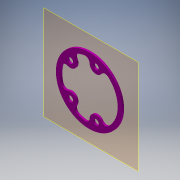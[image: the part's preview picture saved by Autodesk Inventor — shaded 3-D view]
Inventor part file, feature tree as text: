
AUTODESK INVENTOR PART (.ipt)
format: ipt  version: 2017 (Build 210142000, 142)  size: 202,752 bytes
history: native  units: in
note: dims shown in document units (in); Inventor stores cm internally (conversion verified against a paired STEP export)
features: other x4, reference x3, extrude x2, sketch x2, plane x1, fillet x1
ambient origin geometry x8: Origin, YZ Plane, XZ Plane, XY Plane, X Axis, Y Axis, Z Axis, Center Point
bodies: Solid1 (feature_tree)
feature tree (13):
  plane  "Work Plane1"
  extrude  "Extrusion1"  Depth=0.1in
  fillet  "Fillet1"  Radius=0.1in
  extrude  "Extrusion2"  Depth=0.085in
  sketch  "Sketch1"  dims[d0=0.1in d1=0.1in d2=0.1in]
  reference  "Reference1"
  reference  "Reference2"
  sketch  "Sketch2"  dims[d3=0.1in d4=0.15in d5=0.1in d6=0.15in d7=0.05in d8=0.125in d9=0.1in d10=0.125in d11=0.125in d12=0.125in d13=0.125in d14=0.05in d15=0.0in d16=0.125in d17=0.02in d18=0.085in d19=0.0in]
  reference  "Reference3"
  other  "<userpath>\Documents\Inventor\PixyCam and Gimbal\Assembly2.iam"
  other  "Assembly2.iam"
  other  "LEDRing:1"
  other  "frontCase:1"
